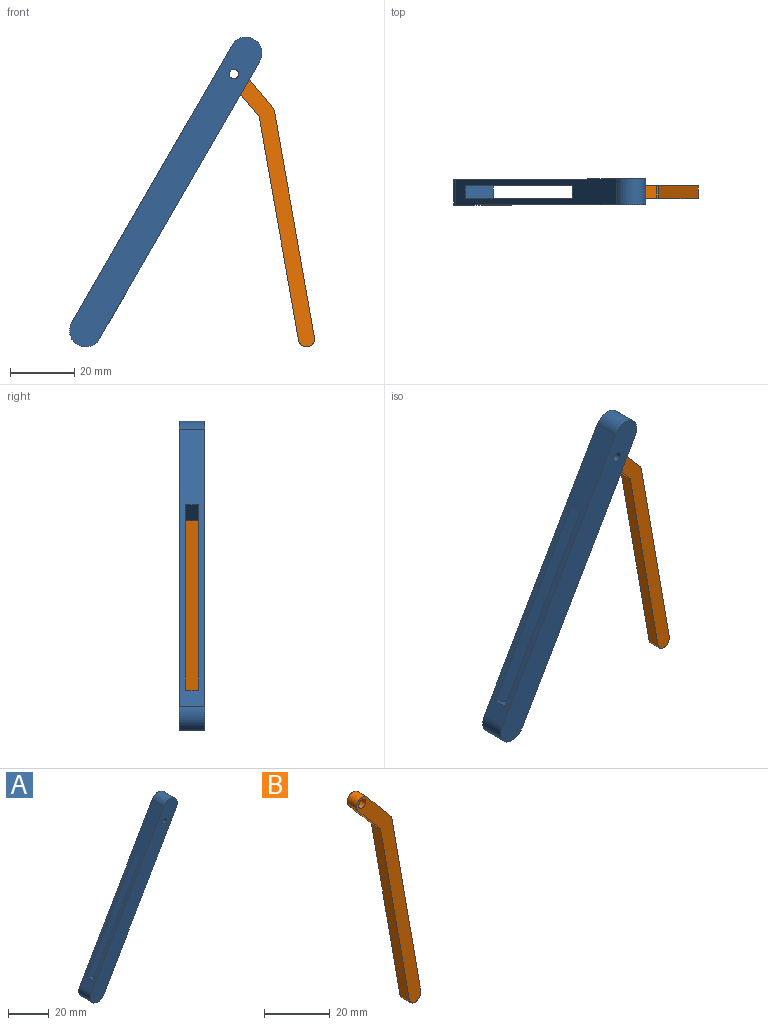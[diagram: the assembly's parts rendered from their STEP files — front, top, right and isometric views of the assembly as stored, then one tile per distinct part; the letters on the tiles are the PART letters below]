
ASSEMBLY  parts=2 mates=1
PART A: 17 faces, bbox 60x8x96.6 mm
  f0: cylinder r=1.5mm len=3mm, axis (0,1,0), area 18.8mm2, adj f7,f10
  f1: cylinder r=5mm len=9.33mm, axis (0,1,0), area 125.7mm2, adj f2,f5,f6,f7
  f2: plane 86.6x50mm, normal (0.87,0,-0.5), area 475mm2, adj f1,f3,f6,f7,f8,f9,f10,f12
  f3: cylinder r=5mm len=9.33mm, axis (0,1,0), area 125.7mm2, adj f2,f5,f6,f7
  f4: cylinder r=1.5mm len=3mm, axis (0,1,0), area 18.8mm2, adj f6,f8
  f5: plane 86.6x50mm, normal (-0.87,0,0.5), area 533mm2, adj f1,f3,f6,f7,f13,f14,f15,f16
  f6: plane 96.6x60mm, normal (0,-1,0), area 1071.5mm2, adj f1,f2,f3,f4,f5
  f7: plane 96.6x60mm, normal (0,1,0), area 1071.5mm2, adj f0,f1,f2,f3,f5
  f8: plane 18.03x7.25mm, normal (0,1,0), area 63mm2, adj f2,f4,f9,f11,f12
  f9: plane 16.08x4mm, normal (1,0,0), area 64.3mm2, adj f2,f8,f10,f11
  f10: plane 18.03x7.25mm, normal (0,-1,0), area 63mm2, adj f0,f2,f9,f11,f12
  f11: plane 4x2.66mm, normal (0.59,0,-0.81), area 13.2mm2, adj f8,f9,f10,f12
  f12: plane 5.47x4.59mm, normal (-0.77,0,-0.64), area 28.6mm2, adj f2,f8,f10,f11
  f13: plane 62.81x42.03mm, normal (0,-1,0), area 667.5mm2, adj f2,f5,f14,f16
  f14: plane 8.66x5mm, normal (-0.5,0,-0.87), area 40mm2, adj f2,f5,f13,f15
  f15: plane 62.81x42.03mm, normal (0,1,0), area 667.5mm2, adj f2,f5,f14,f16
  f16: plane 8.66x5mm, normal (0.5,0,0.87), area 40mm2, adj f2,f5,f13,f15
PART B: 10 faces, bbox 27.6x4x87.6 mm
  f0: plane 11.67x9.79mm, normal (-0.77,0,-0.64), area 61mm2, adj f1,f6,f8,f9
  f1: plane 69.74x12.3mm, normal (-0.98,0,-0.17), area 283.3mm2, adj f0,f2,f8,f9
  f2: cylinder r=2.5mm len=4.96mm, axis (0,1,0), area 31.4mm2, adj f1,f3,f8,f9
  f3: plane 70.4x12.41mm, normal (0.98,0,0.17), area 285.9mm2, adj f2,f4,f8,f9
  f4: cylinder r=2.5mm len=4mm, axis (0,1,0), area 5.2mm2, adj f3,f5,f8,f9
  f5: plane 12.19x10.23mm, normal (0.77,0,0.64), area 63.6mm2, adj f4,f6,f8,f9
  f6: cylinder r=2.5mm len=4.42mm, axis (0,1,0), area 31.4mm2, adj f0,f5,f8,f9
  f7: cylinder r=1.5mm len=4mm, axis (0,1,0), area 37.7mm2, adj f8,f9
  f8: plane 87.59x27.64mm, normal (0,-1,0), area 449.5mm2, adj f0,f1,f2,f3,f4,f5,f6,f7
  f9: plane 87.59x27.64mm, normal (0,1,0), area 449.5mm2, adj f0,f1,f2,f3,f4,f5,f6,f7
PLACE A at identity fixed
PLACE B rot(axis=(0,-1,0),0deg) t=(0.58,0,1.46)mm
MATE revolute B.f6 <-> A.f0  axis (0,1,0) through (46.24,0,80.09)mm
